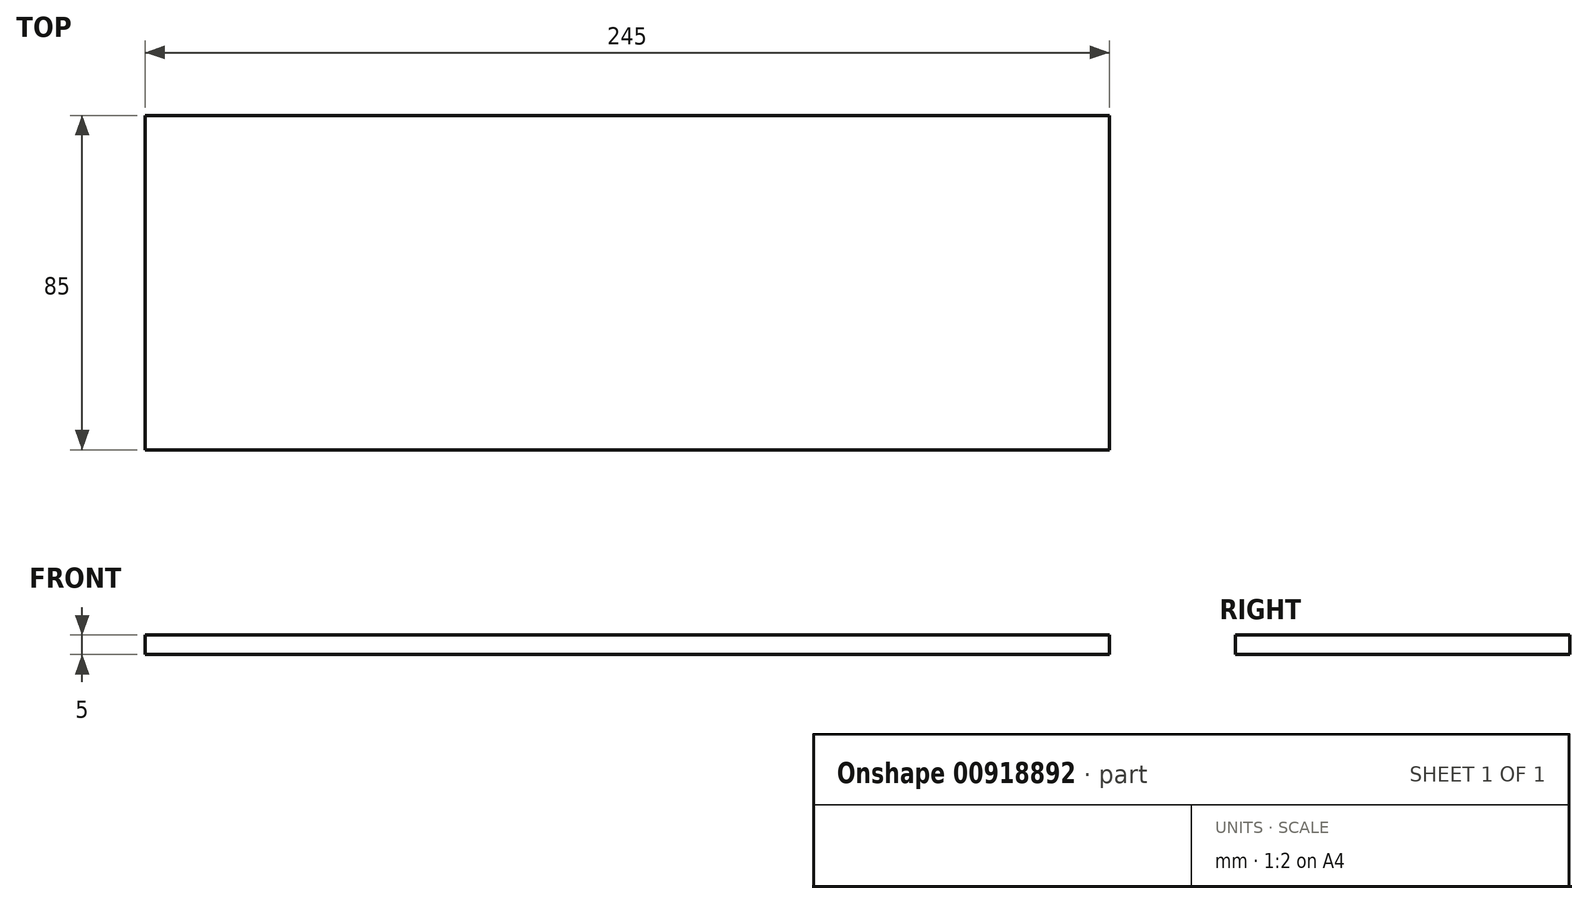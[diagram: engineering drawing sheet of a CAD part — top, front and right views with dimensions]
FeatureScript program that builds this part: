
annotation { "Feature Type Name" : "Feature", "Feature Type Description" : "" }
export const myFeature = defineFeature(function(context is Context, id is Id, definition is map)
    precondition{}
    {
        {
            var Q0;
            Q0=qCreatedBy(makeId("Top.planeOp"),FACE);
            var sketch = newSketch(context, id + "F0", { "sketchPlane" : qUnion([Q0])});
            skLineSegment(sketch, "E0.bottom", {"start": v(-128.08, 21.98) * mm, "end": v(116.92, 21.98) * mm});
            skLineSegment(sketch, "E0.top", {"start": v(-128.08, -63.02) * mm, "end": v(116.92, -63.02) * mm});
            skLineSegment(sketch, "E0.left", {"start": v(-128.08, 21.98) * mm, "end": v(-128.08, -63.02) * mm});
            skLineSegment(sketch, "E0.right", {"start": v(116.92, 21.98) * mm, "end": v(116.92, -63.02) * mm});
            skSolve(sketch);
        }
        {
            var Q0;
            Q0=makeQuery(id+"F0.imprint","IMPRINT",FACE,{"disambiguationData":[TD([[makeQuery(id+"F0.imprint","IMPRINT",EDGE,{"derivedFrom":sQuery(id+"F0.wireOp",EDGE,"E0.bottom")}),-1.0]])]});
            extrude(context, id + "F1", {"entities" : qUnion([Q0]), "depth" : 5 * mm, "offsetDistance" : 25 * mm});
        }
    });
